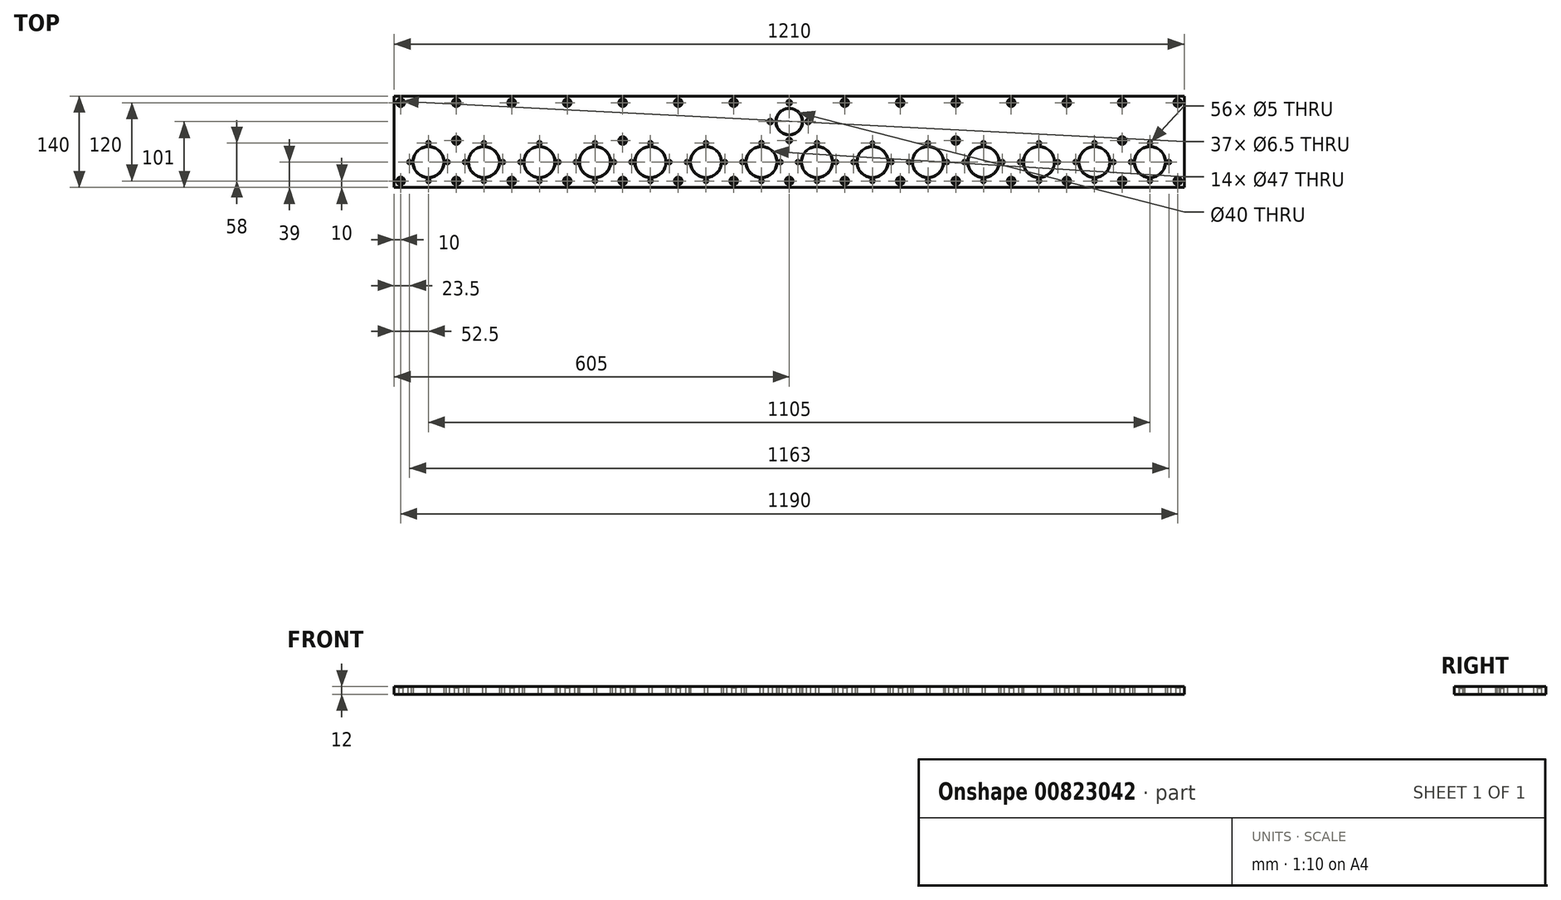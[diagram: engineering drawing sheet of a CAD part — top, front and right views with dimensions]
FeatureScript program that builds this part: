
annotation { "Feature Type Name" : "Feature", "Feature Type Description" : "" }
export const myFeature = defineFeature(function(context is Context, id is Id, definition is map)
    precondition{}
    {
        {
            var Q0;
            Q0=qCreatedBy(makeId("Top.planeOp"),FACE);
            var sketch = newSketch(context, id + "F0", { "sketchPlane" : qUnion([Q0])});
            skCircle(sketch, "E0", {"center": v(0, 0) * mm, "radius": 23.5 * mm, "construction": true});
            skLineSegment(sketch, "E1", {"start": v(0, 0) * mm, "end": v(1572.14, 0) * mm, "construction": true});
            skLineSegment(sketch, "E2", {"start": v(0, 0) * mm, "end": v(0, 543.6) * mm, "construction": true});
            skCircle(sketch, "E3", {"center": v(-42.5, -62) * mm, "radius": 23.5 * mm});
            skCircle(sketch, "E4", {"center": v(-42.5, -62) * mm, "radius": 37.5 * mm, "construction": true});
            skCircle(sketch, "E5", {"center": v(0, 0) * mm, "radius": 37.5 * mm, "construction": true});
            skCircle(sketch, "E6", {"center": v(-42.5, -62) * mm, "radius": 29 * mm, "construction": true});
            skCircle(sketch, "E7", {"center": v(0, 0) * mm, "radius": 29 * mm, "construction": true});
            skLineSegment(sketch, "E8", {"start": v(-42.5, -62) * mm, "end": v(-42.5, -24.5) * mm, "construction": true});
            skCircle(sketch, "E9", {"center": v(0, 29) * mm, "radius": 2.5 * mm, "construction": true});
            skCircle(sketch, "E10", {"center": v(-42.5, -33) * mm, "radius": 2.5 * mm});
            skCircle(sketch, "E11.1.0", {"center": v(-29, 0) * mm, "radius": 2.5 * mm, "construction": true});
            skCircle(sketch, "E11.2.0", {"center": v(0, -29) * mm, "radius": 2.5 * mm, "construction": true});
            skCircle(sketch, "E11.3.0", {"center": v(29, 0) * mm, "radius": 2.5 * mm, "construction": true});
            skLineSegment(sketch, "E12", {"start": v(-42.5, -62) * mm, "end": v(-80, -62) * mm, "construction": true});
            skLineSegment(sketch, "E13", {"start": v(-42.5, -62) * mm, "end": v(-42.5, -99.5) * mm, "construction": true});
            skLineSegment(sketch, "E14", {"start": v(-42.5, -62) * mm, "end": v(-5, -62) * mm, "construction": true});
            skCircle(sketch, "E15", {"center": v(-13.5, -62) * mm, "radius": 2.5 * mm});
            skCircle(sketch, "E16", {"center": v(-42.5, -91) * mm, "radius": 2.5 * mm});
            skCircle(sketch, "E17", {"center": v(-71.5, -62) * mm, "radius": 2.5 * mm});
            skCircle(sketch, "E18.MirrorC", {"center": v(42.5, -91) * mm, "radius": 2.5 * mm});
            skCircle(sketch, "E19.MirrorC", {"center": v(71.5, -62) * mm, "radius": 2.5 * mm});
            skCircle(sketch, "E20.MirrorC", {"center": v(42.5, -33) * mm, "radius": 2.5 * mm});
            skCircle(sketch, "E21.MirrorC", {"center": v(13.5, -62) * mm, "radius": 2.5 * mm});
            skCircle(sketch, "E22.MirrorC", {"center": v(42.5, -62) * mm, "radius": 23.5 * mm});
            skPoint(sketch, "E23.1.0.0", {"position": v(-85, 0) * mm});
            skCircle(sketch, "E23.1.0.1", {"center": v(-85, 0) * mm, "radius": 23.5 * mm, "construction": true});
            skCircle(sketch, "E23.1.0.2", {"center": v(-127.5, -62) * mm, "radius": 23.5 * mm});
            skCircle(sketch, "E23.1.0.3", {"center": v(-98.5, -62) * mm, "radius": 2.5 * mm});
            skCircle(sketch, "E23.1.0.4", {"center": v(-156.5, -62) * mm, "radius": 2.5 * mm});
            skCircle(sketch, "E23.1.0.5", {"center": v(-127.5, -91) * mm, "radius": 2.5 * mm});
            skCircle(sketch, "E23.1.0.6", {"center": v(-56, 0) * mm, "radius": 2.5 * mm, "construction": true});
            skCircle(sketch, "E23.1.0.7", {"center": v(-85, 29) * mm, "radius": 2.5 * mm, "construction": true});
            skCircle(sketch, "E23.1.0.8", {"center": v(-85, -29) * mm, "radius": 2.5 * mm, "construction": true});
            skCircle(sketch, "E23.1.0.9", {"center": v(-127.5, -33) * mm, "radius": 2.5 * mm});
            skCircle(sketch, "E23.1.0.10", {"center": v(-114, 0) * mm, "radius": 2.5 * mm, "construction": true});
            skPoint(sketch, "E23.2.0.0", {"position": v(-170, 0) * mm});
            skCircle(sketch, "E23.2.0.1", {"center": v(-170, 0) * mm, "radius": 23.5 * mm, "construction": true});
            skCircle(sketch, "E23.2.0.2", {"center": v(-212.5, -62) * mm, "radius": 23.5 * mm});
            skCircle(sketch, "E23.2.0.3", {"center": v(-183.5, -62) * mm, "radius": 2.5 * mm});
            skCircle(sketch, "E23.2.0.4", {"center": v(-241.5, -62) * mm, "radius": 2.5 * mm});
            skCircle(sketch, "E23.2.0.5", {"center": v(-212.5, -91) * mm, "radius": 2.5 * mm});
            skCircle(sketch, "E23.2.0.6", {"center": v(-141, 0) * mm, "radius": 2.5 * mm, "construction": true});
            skCircle(sketch, "E23.2.0.7", {"center": v(-170, 29) * mm, "radius": 2.5 * mm, "construction": true});
            skCircle(sketch, "E23.2.0.8", {"center": v(-170, -29) * mm, "radius": 2.5 * mm, "construction": true});
            skCircle(sketch, "E23.2.0.9", {"center": v(-212.5, -33) * mm, "radius": 2.5 * mm});
            skCircle(sketch, "E23.2.0.10", {"center": v(-199, 0) * mm, "radius": 2.5 * mm, "construction": true});
            skPoint(sketch, "E23.3.0.0", {"position": v(-255, 0) * mm});
            skCircle(sketch, "E23.3.0.1", {"center": v(-255, 0) * mm, "radius": 23.5 * mm, "construction": true});
            skCircle(sketch, "E23.3.0.2", {"center": v(-297.5, -62) * mm, "radius": 23.5 * mm});
            skCircle(sketch, "E23.3.0.3", {"center": v(-268.5, -62) * mm, "radius": 2.5 * mm});
            skCircle(sketch, "E23.3.0.4", {"center": v(-326.5, -62) * mm, "radius": 2.5 * mm});
            skCircle(sketch, "E23.3.0.5", {"center": v(-297.5, -91) * mm, "radius": 2.5 * mm});
            skCircle(sketch, "E23.3.0.6", {"center": v(-226, 0) * mm, "radius": 2.5 * mm, "construction": true});
            skCircle(sketch, "E23.3.0.7", {"center": v(-255, 29) * mm, "radius": 2.5 * mm, "construction": true});
            skCircle(sketch, "E23.3.0.8", {"center": v(-255, -29) * mm, "radius": 2.5 * mm, "construction": true});
            skCircle(sketch, "E23.3.0.9", {"center": v(-297.5, -33) * mm, "radius": 2.5 * mm});
            skCircle(sketch, "E23.3.0.10", {"center": v(-284, 0) * mm, "radius": 2.5 * mm, "construction": true});
            skPoint(sketch, "E23.4.0.0", {"position": v(-340, 0) * mm});
            skCircle(sketch, "E23.4.0.1", {"center": v(-340, 0) * mm, "radius": 23.5 * mm, "construction": true});
            skCircle(sketch, "E23.4.0.2", {"center": v(-382.5, -62) * mm, "radius": 23.5 * mm});
            skCircle(sketch, "E23.4.0.3", {"center": v(-353.5, -62) * mm, "radius": 2.5 * mm});
            skCircle(sketch, "E23.4.0.4", {"center": v(-411.5, -62) * mm, "radius": 2.5 * mm});
            skCircle(sketch, "E23.4.0.5", {"center": v(-382.5, -91) * mm, "radius": 2.5 * mm});
            skCircle(sketch, "E23.4.0.6", {"center": v(-311, 0) * mm, "radius": 2.5 * mm, "construction": true});
            skCircle(sketch, "E23.4.0.7", {"center": v(-340, 29) * mm, "radius": 2.5 * mm, "construction": true});
            skCircle(sketch, "E23.4.0.8", {"center": v(-340, -29) * mm, "radius": 2.5 * mm, "construction": true});
            skCircle(sketch, "E23.4.0.9", {"center": v(-382.5, -33) * mm, "radius": 2.5 * mm});
            skCircle(sketch, "E23.4.0.10", {"center": v(-369, 0) * mm, "radius": 2.5 * mm, "construction": true});
            skPoint(sketch, "E23.5.0.0", {"position": v(-425, 0) * mm});
            skCircle(sketch, "E23.5.0.1", {"center": v(-425, 0) * mm, "radius": 23.5 * mm, "construction": true});
            skCircle(sketch, "E23.5.0.2", {"center": v(-467.5, -62) * mm, "radius": 23.5 * mm});
            skCircle(sketch, "E23.5.0.3", {"center": v(-438.5, -62) * mm, "radius": 2.5 * mm});
            skCircle(sketch, "E23.5.0.4", {"center": v(-496.5, -62) * mm, "radius": 2.5 * mm});
            skCircle(sketch, "E23.5.0.5", {"center": v(-467.5, -91) * mm, "radius": 2.5 * mm});
            skCircle(sketch, "E23.5.0.6", {"center": v(-396, 0) * mm, "radius": 2.5 * mm, "construction": true});
            skCircle(sketch, "E23.5.0.7", {"center": v(-425, 29) * mm, "radius": 2.5 * mm, "construction": true});
            skCircle(sketch, "E23.5.0.8", {"center": v(-425, -29) * mm, "radius": 2.5 * mm, "construction": true});
            skCircle(sketch, "E23.5.0.9", {"center": v(-467.5, -33) * mm, "radius": 2.5 * mm});
            skCircle(sketch, "E23.5.0.10", {"center": v(-454, 0) * mm, "radius": 2.5 * mm, "construction": true});
            skPoint(sketch, "E23.6.0.0", {"position": v(-510, 0) * mm});
            skCircle(sketch, "E23.6.0.1", {"center": v(-510, 0) * mm, "radius": 23.5 * mm, "construction": true});
            skCircle(sketch, "E23.6.0.2", {"center": v(-552.5, -62) * mm, "radius": 23.5 * mm});
            skCircle(sketch, "E23.6.0.3", {"center": v(-523.5, -62) * mm, "radius": 2.5 * mm});
            skCircle(sketch, "E23.6.0.4", {"center": v(-581.5, -62) * mm, "radius": 2.5 * mm});
            skCircle(sketch, "E23.6.0.5", {"center": v(-552.5, -91) * mm, "radius": 2.5 * mm});
            skCircle(sketch, "E23.6.0.6", {"center": v(-481, 0) * mm, "radius": 2.5 * mm, "construction": true});
            skCircle(sketch, "E23.6.0.7", {"center": v(-510, 29) * mm, "radius": 2.5 * mm, "construction": true});
            skCircle(sketch, "E23.6.0.8", {"center": v(-510, -29) * mm, "radius": 2.5 * mm, "construction": true});
            skCircle(sketch, "E23.6.0.9", {"center": v(-552.5, -33) * mm, "radius": 2.5 * mm});
            skCircle(sketch, "E23.6.0.10", {"center": v(-539, 0) * mm, "radius": 2.5 * mm, "construction": true});
            skLineSegment(sketch, "E23.direction1", {"start": v(-42.5, -91) * mm, "end": v(-127.5, -91) * mm, "construction": true});
            skCircle(sketch, "E24.1.0.0", {"center": v(85, 0) * mm, "radius": 23.5 * mm, "construction": true});
            skCircle(sketch, "E24.1.0.1", {"center": v(85, -29) * mm, "radius": 2.5 * mm, "construction": true});
            skCircle(sketch, "E24.1.0.2", {"center": v(56, 0) * mm, "radius": 2.5 * mm, "construction": true});
            skCircle(sketch, "E24.1.0.3", {"center": v(85, 29) * mm, "radius": 2.5 * mm, "construction": true});
            skCircle(sketch, "E24.1.0.4", {"center": v(114, 0) * mm, "radius": 2.5 * mm, "construction": true});
            skCircle(sketch, "E24.1.0.5", {"center": v(127.5, -33) * mm, "radius": 2.5 * mm});
            skCircle(sketch, "E24.1.0.6", {"center": v(98.5, -62) * mm, "radius": 2.5 * mm});
            skCircle(sketch, "E24.1.0.7", {"center": v(127.5, -62) * mm, "radius": 23.5 * mm});
            skCircle(sketch, "E24.1.0.8", {"center": v(156.5, -62) * mm, "radius": 2.5 * mm});
            skCircle(sketch, "E24.1.0.9", {"center": v(127.5, -91) * mm, "radius": 2.5 * mm});
            skCircle(sketch, "E24.2.0.0", {"center": v(170, 0) * mm, "radius": 23.5 * mm, "construction": true});
            skCircle(sketch, "E24.2.0.1", {"center": v(170, -29) * mm, "radius": 2.5 * mm, "construction": true});
            skCircle(sketch, "E24.2.0.2", {"center": v(141, 0) * mm, "radius": 2.5 * mm, "construction": true});
            skCircle(sketch, "E24.2.0.3", {"center": v(170, 29) * mm, "radius": 2.5 * mm, "construction": true});
            skCircle(sketch, "E24.2.0.4", {"center": v(199, 0) * mm, "radius": 2.5 * mm, "construction": true});
            skCircle(sketch, "E24.2.0.5", {"center": v(212.5, -33) * mm, "radius": 2.5 * mm});
            skCircle(sketch, "E24.2.0.6", {"center": v(183.5, -62) * mm, "radius": 2.5 * mm});
            skCircle(sketch, "E24.2.0.7", {"center": v(212.5, -62) * mm, "radius": 23.5 * mm});
            skCircle(sketch, "E24.2.0.8", {"center": v(241.5, -62) * mm, "radius": 2.5 * mm});
            skCircle(sketch, "E24.2.0.9", {"center": v(212.5, -91) * mm, "radius": 2.5 * mm});
            skCircle(sketch, "E24.3.0.0", {"center": v(255, 0) * mm, "radius": 23.5 * mm, "construction": true});
            skCircle(sketch, "E24.3.0.1", {"center": v(255, -29) * mm, "radius": 2.5 * mm, "construction": true});
            skCircle(sketch, "E24.3.0.2", {"center": v(226, 0) * mm, "radius": 2.5 * mm, "construction": true});
            skCircle(sketch, "E24.3.0.3", {"center": v(255, 29) * mm, "radius": 2.5 * mm, "construction": true});
            skCircle(sketch, "E24.3.0.4", {"center": v(284, 0) * mm, "radius": 2.5 * mm, "construction": true});
            skCircle(sketch, "E24.3.0.5", {"center": v(297.5, -33) * mm, "radius": 2.5 * mm});
            skCircle(sketch, "E24.3.0.6", {"center": v(268.5, -62) * mm, "radius": 2.5 * mm});
            skCircle(sketch, "E24.3.0.7", {"center": v(297.5, -62) * mm, "radius": 23.5 * mm});
            skCircle(sketch, "E24.3.0.8", {"center": v(326.5, -62) * mm, "radius": 2.5 * mm});
            skCircle(sketch, "E24.3.0.9", {"center": v(297.5, -91) * mm, "radius": 2.5 * mm});
            skCircle(sketch, "E24.4.0.0", {"center": v(340, 0) * mm, "radius": 23.5 * mm, "construction": true});
            skCircle(sketch, "E24.4.0.1", {"center": v(340, -29) * mm, "radius": 2.5 * mm, "construction": true});
            skCircle(sketch, "E24.4.0.2", {"center": v(311, 0) * mm, "radius": 2.5 * mm, "construction": true});
            skCircle(sketch, "E24.4.0.3", {"center": v(340, 29) * mm, "radius": 2.5 * mm, "construction": true});
            skCircle(sketch, "E24.4.0.4", {"center": v(369, 0) * mm, "radius": 2.5 * mm, "construction": true});
            skCircle(sketch, "E24.4.0.5", {"center": v(382.5, -33) * mm, "radius": 2.5 * mm});
            skCircle(sketch, "E24.4.0.6", {"center": v(353.5, -62) * mm, "radius": 2.5 * mm});
            skCircle(sketch, "E24.4.0.7", {"center": v(382.5, -62) * mm, "radius": 23.5 * mm});
            skCircle(sketch, "E24.4.0.8", {"center": v(411.5, -62) * mm, "radius": 2.5 * mm});
            skCircle(sketch, "E24.4.0.9", {"center": v(382.5, -91) * mm, "radius": 2.5 * mm});
            skCircle(sketch, "E24.5.0.0", {"center": v(425, 0) * mm, "radius": 23.5 * mm, "construction": true});
            skCircle(sketch, "E24.5.0.1", {"center": v(425, -29) * mm, "radius": 2.5 * mm, "construction": true});
            skCircle(sketch, "E24.5.0.2", {"center": v(396, 0) * mm, "radius": 2.5 * mm, "construction": true});
            skCircle(sketch, "E24.5.0.3", {"center": v(425, 29) * mm, "radius": 2.5 * mm, "construction": true});
            skCircle(sketch, "E24.5.0.4", {"center": v(454, 0) * mm, "radius": 2.5 * mm, "construction": true});
            skCircle(sketch, "E24.5.0.5", {"center": v(467.5, -33) * mm, "radius": 2.5 * mm});
            skCircle(sketch, "E24.5.0.6", {"center": v(438.5, -62) * mm, "radius": 2.5 * mm});
            skCircle(sketch, "E24.5.0.7", {"center": v(467.5, -62) * mm, "radius": 23.5 * mm});
            skCircle(sketch, "E24.5.0.8", {"center": v(496.5, -62) * mm, "radius": 2.5 * mm});
            skCircle(sketch, "E24.5.0.9", {"center": v(467.5, -91) * mm, "radius": 2.5 * mm});
            skCircle(sketch, "E24.6.0.0", {"center": v(510, 0) * mm, "radius": 23.5 * mm, "construction": true});
            skCircle(sketch, "E24.6.0.1", {"center": v(510, -29) * mm, "radius": 2.5 * mm, "construction": true});
            skCircle(sketch, "E24.6.0.2", {"center": v(481, 0) * mm, "radius": 2.5 * mm, "construction": true});
            skCircle(sketch, "E24.6.0.3", {"center": v(510, 29) * mm, "radius": 2.5 * mm, "construction": true});
            skCircle(sketch, "E24.6.0.4", {"center": v(539, 0) * mm, "radius": 2.5 * mm, "construction": true});
            skCircle(sketch, "E24.6.0.5", {"center": v(552.5, -33) * mm, "radius": 2.5 * mm});
            skCircle(sketch, "E24.6.0.6", {"center": v(523.5, -62) * mm, "radius": 2.5 * mm});
            skCircle(sketch, "E24.6.0.7", {"center": v(552.5, -62) * mm, "radius": 23.5 * mm});
            skCircle(sketch, "E24.6.0.8", {"center": v(581.5, -62) * mm, "radius": 2.5 * mm});
            skCircle(sketch, "E24.6.0.9", {"center": v(552.5, -91) * mm, "radius": 2.5 * mm});
            skLineSegment(sketch, "E24.direction1", {"start": v(42.5, -91) * mm, "end": v(127.5, -91) * mm, "construction": true});
            skLineSegment(sketch, "E25.bottom", {"start": v(605, -101) * mm, "end": v(-605, -101) * mm});
            skLineSegment(sketch, "E25.top", {"start": v(605, 39) * mm, "end": v(-605, 39) * mm});
            skLineSegment(sketch, "E25.left", {"start": v(605, -101) * mm, "end": v(605, 39) * mm});
            skLineSegment(sketch, "E25.right", {"start": v(-605, -101) * mm, "end": v(-605, 39) * mm});
            skPoint(sketch, "E25.middle", {"position": v(0, -31) * mm});
            skLineSegment(sketch, "E26", {"start": v(-552.5, -62) * mm, "end": v(-510, 0) * mm, "construction": true});
            skLineSegment(sketch, "E27", {"start": v(-467.5, -62) * mm, "end": v(-510, 0) * mm, "construction": true});
            skLineSegment(sketch, "E28", {"start": v(-531.25, -31) * mm, "end": v(605, -31) * mm, "construction": true});
            skPoint(sketch, "E29.orphan", {"position": v(-488.75, -31) * mm});
            skCircle(sketch, "E30.MirrorC", {"center": v(-510, -91) * mm, "radius": 2.5 * mm, "construction": true});
            skCircle(sketch, "E31.MirrorC", {"center": v(-425, -91) * mm, "radius": 2.5 * mm, "construction": true});
            skLineSegment(sketch, "E32", {"start": v(-552.5, -62) * mm, "end": v(-552.5, 29.1) * mm, "construction": true});
            skCircle(sketch, "E33.MirrorC", {"center": v(-595, 29) * mm, "radius": 2.5 * mm, "construction": true});
            skCircle(sketch, "E34.MirrorC", {"center": v(-595, -91) * mm, "radius": 2.5 * mm, "construction": true});
            skCircle(sketch, "E35", {"center": v(-595, 29) * mm, "radius": 6 * mm, "construction": true});
            skCircle(sketch, "E36", {"center": v(-552.5, -62) * mm, "radius": 37 * mm, "construction": true});
            skCircle(sketch, "E37.MirrorC", {"center": v(510, -91) * mm, "radius": 2.5 * mm, "construction": true});
            skCircle(sketch, "E38.MirrorC", {"center": v(425, -91) * mm, "radius": 2.5 * mm, "construction": true});
            skLineSegment(sketch, "E39", {"start": v(552.5, -62) * mm, "end": v(552.5, 52.17) * mm, "construction": true});
            skCircle(sketch, "E40.MirrorC", {"center": v(595, 29) * mm, "radius": 2.5 * mm, "construction": true});
            skCircle(sketch, "E41.MirrorC", {"center": v(595, -91) * mm, "radius": 2.5 * mm, "construction": true});
            skCircle(sketch, "E42.MirrorC", {"center": v(340, -91) * mm, "radius": 2.5 * mm, "construction": true});
            skCircle(sketch, "E43.MirrorC", {"center": v(255, -91) * mm, "radius": 2.5 * mm, "construction": true});
            skCircle(sketch, "E44.MirrorC", {"center": v(170, -91) * mm, "radius": 2.5 * mm, "construction": true});
            skCircle(sketch, "E45.MirrorC", {"center": v(85, -91) * mm, "radius": 2.5 * mm, "construction": true});
            skCircle(sketch, "E46.MirrorC", {"center": v(0, -91) * mm, "radius": 2.5 * mm, "construction": true});
            skCircle(sketch, "E47.MirrorC", {"center": v(-85, -91) * mm, "radius": 2.5 * mm, "construction": true});
            skCircle(sketch, "E48.MirrorC", {"center": v(-170, -91) * mm, "radius": 2.5 * mm, "construction": true});
            skCircle(sketch, "E49.MirrorC", {"center": v(-255, -91) * mm, "radius": 2.5 * mm, "construction": true});
            skCircle(sketch, "E50.MirrorC", {"center": v(-340, -91) * mm, "radius": 2.5 * mm, "construction": true});
            skCircle(sketch, "E51", {"center": v(-595, 29) * mm, "radius": 3.25 * mm});
            skCircle(sketch, "E52", {"center": v(-595, -91) * mm, "radius": 3.25 * mm});
            skCircle(sketch, "E53.1.0.0", {"center": v(-510, 29) * mm, "radius": 3.25 * mm});
            skCircle(sketch, "E53.1.0.1", {"center": v(-510, -91) * mm, "radius": 3.25 * mm});
            skCircle(sketch, "E53.2.0.0", {"center": v(-425, 29) * mm, "radius": 3.25 * mm});
            skCircle(sketch, "E53.2.0.1", {"center": v(-425, -91) * mm, "radius": 3.25 * mm});
            skCircle(sketch, "E53.3.0.0", {"center": v(-340, 29) * mm, "radius": 3.25 * mm});
            skCircle(sketch, "E53.3.0.1", {"center": v(-340, -91) * mm, "radius": 3.25 * mm});
            skCircle(sketch, "E53.4.0.0", {"center": v(-255, 29) * mm, "radius": 3.25 * mm});
            skCircle(sketch, "E53.4.0.1", {"center": v(-255, -91) * mm, "radius": 3.25 * mm});
            skCircle(sketch, "E53.5.0.0", {"center": v(-170, 29) * mm, "radius": 3.25 * mm});
            skCircle(sketch, "E53.5.0.1", {"center": v(-170, -91) * mm, "radius": 3.25 * mm});
            skCircle(sketch, "E53.6.0.0", {"center": v(-85, 29) * mm, "radius": 3.25 * mm});
            skCircle(sketch, "E53.6.0.1", {"center": v(-85, -91) * mm, "radius": 3.25 * mm});
            skCircle(sketch, "E53.7.0.0", {"center": v(0, 29) * mm, "radius": 3.25 * mm});
            skCircle(sketch, "E53.7.0.1", {"center": v(0, -91) * mm, "radius": 3.25 * mm});
            skCircle(sketch, "E53.8.0.0", {"center": v(85, 29) * mm, "radius": 3.25 * mm});
            skCircle(sketch, "E53.8.0.1", {"center": v(85, -91) * mm, "radius": 3.25 * mm});
            skCircle(sketch, "E53.9.0.0", {"center": v(170, 29) * mm, "radius": 3.25 * mm});
            skCircle(sketch, "E53.9.0.1", {"center": v(170, -91) * mm, "radius": 3.25 * mm});
            skCircle(sketch, "E53.10.0.0", {"center": v(255, 29) * mm, "radius": 3.25 * mm});
            skCircle(sketch, "E53.10.0.1", {"center": v(255, -91) * mm, "radius": 3.25 * mm});
            skCircle(sketch, "E53.11.0.0", {"center": v(340, 29) * mm, "radius": 3.25 * mm});
            skCircle(sketch, "E53.11.0.1", {"center": v(340, -91) * mm, "radius": 3.25 * mm});
            skCircle(sketch, "E53.12.0.0", {"center": v(425, 29) * mm, "radius": 3.25 * mm});
            skCircle(sketch, "E53.12.0.1", {"center": v(425, -91) * mm, "radius": 3.25 * mm});
            skCircle(sketch, "E53.13.0.0", {"center": v(510, 29) * mm, "radius": 3.25 * mm});
            skCircle(sketch, "E53.13.0.1", {"center": v(510, -91) * mm, "radius": 3.25 * mm});
            skCircle(sketch, "E53.14.0.0", {"center": v(595, 29) * mm, "radius": 3.25 * mm});
            skCircle(sketch, "E53.14.0.1", {"center": v(595, -91) * mm, "radius": 3.25 * mm});
            skLineSegment(sketch, "E53.direction1", {"start": v(-595, -91) * mm, "end": v(-510, -91) * mm, "construction": true});
            skCircle(sketch, "E54", {"center": v(-510, -29) * mm, "radius": 3.25 * mm});
            skCircle(sketch, "E55", {"center": v(0, -29) * mm, "radius": 3.25 * mm});
            skCircle(sketch, "E56", {"center": v(510, -29) * mm, "radius": 3.25 * mm});
            skCircle(sketch, "E57", {"center": v(255, -29) * mm, "radius": 3.25 * mm});
            skCircle(sketch, "E58", {"center": v(-255, -29) * mm, "radius": 3.25 * mm});
            skCircle(sketch, "E59", {"center": v(-29, 0) * mm, "radius": 3.25 * mm});
            skCircle(sketch, "E60", {"center": v(29, 0) * mm, "radius": 3.25 * mm});
            skCircle(sketch, "E61", {"center": v(0, 0) * mm, "radius": 20 * mm});
            skSolve(sketch);
        }
        {
            var Q0;
            Q0=qSketchRegion(id+"F0",true);
            extrude(context, id + "F1", {"entities" : qUnion([Q0]), "depth" : 12 * mm, "offsetDistance" : 25 * mm});
        }
        {
            var Q0;
            Q0=makeQuery(id+"F1.opExtrude","SWEPT_FACE",FACE,{"disambiguationData":[OSD([sQuery(id+"F0.wireOp",EDGE,"E24.6.0.7")])]});
            var Q1;
            Q1=makeQuery(id+"F1.opExtrude","SWEPT_FACE",FACE,{"disambiguationData":[OSD([sQuery(id+"F0.wireOp",EDGE,"E24.6.0.6")])]});
            var Q2;
            Q2=makeQuery(id+"F1.opExtrude","SWEPT_FACE",FACE,{"disambiguationData":[OSD([sQuery(id+"F0.wireOp",EDGE,"E24.6.0.9")])]});
            var Q3;
            Q3=makeQuery(id+"F1.opExtrude","SWEPT_FACE",FACE,{"disambiguationData":[OSD([sQuery(id+"F0.wireOp",EDGE,"E24.6.0.5")])]});
            var Q4;
            Q4=makeQuery(id+"F1.opExtrude","SWEPT_FACE",FACE,{"disambiguationData":[OSD([sQuery(id+"F0.wireOp",EDGE,"E24.6.0.8")])]});
            var Q5;
            Q5=makeQuery(id+"F1.opExtrude","SWEPT_FACE",FACE,{"disambiguationData":[OSD([sQuery(id+"F0.wireOp",EDGE,"E24.5.0.7")])]});
            var Q6;
            Q6=makeQuery(id+"F1.opExtrude","SWEPT_FACE",FACE,{"disambiguationData":[OSD([sQuery(id+"F0.wireOp",EDGE,"E24.6.0.0")])]});
            var Q7;
            Q7=makeQuery(id+"F1.opExtrude","SWEPT_FACE",FACE,{"disambiguationData":[OSD([sQuery(id+"F0.wireOp",EDGE,"E24.5.0.0")])]});
            var Q8;
            Q8=makeQuery(id+"F1.opExtrude","SWEPT_FACE",FACE,{"disambiguationData":[OSD([sQuery(id+"F0.wireOp",EDGE,"E24.4.0.7")])]});
            var Q9;
            Q9=makeQuery(id+"F1.opExtrude","SWEPT_FACE",FACE,{"disambiguationData":[OSD([sQuery(id+"F0.wireOp",EDGE,"E24.3.0.7")])]});
            var Q10;
            Q10=makeQuery(id+"F1.opExtrude","SWEPT_FACE",FACE,{"disambiguationData":[OSD([sQuery(id+"F0.wireOp",EDGE,"E24.4.0.0")])]});
            var Q11;
            Q11=makeQuery(id+"F1.opExtrude","SWEPT_FACE",FACE,{"disambiguationData":[OSD([sQuery(id+"F0.wireOp",EDGE,"E24.3.0.0")])]});
            var Q12;
            Q12=makeQuery(id+"F1.opExtrude","SWEPT_FACE",FACE,{"disambiguationData":[OSD([sQuery(id+"F0.wireOp",EDGE,"E24.2.0.7")])]});
            var Q13;
            Q13=makeQuery(id+"F1.opExtrude","SWEPT_FACE",FACE,{"disambiguationData":[OSD([sQuery(id+"F0.wireOp",EDGE,"E24.2.0.0")])]});
            var Q14;
            Q14=makeQuery(id+"F1.opExtrude","SWEPT_FACE",FACE,{"disambiguationData":[OSD([sQuery(id+"F0.wireOp",EDGE,"E24.1.0.7")])]});
            var Q15;
            Q15=makeQuery(id+"F1.opExtrude","SWEPT_FACE",FACE,{"disambiguationData":[OSD([sQuery(id+"F0.wireOp",EDGE,"E24.1.0.0")])]});
            var Q16;
            Q16=makeQuery(id+"F1.opExtrude","SWEPT_FACE",FACE,{"disambiguationData":[OSD([sQuery(id+"F0.wireOp",EDGE,"E22.MirrorC")])]});
            var Q17;
            Q17=makeQuery(id+"F1.opExtrude","SWEPT_FACE",FACE,{"disambiguationData":[OSD([sQuery(id+"F0.wireOp",EDGE,"E0")])]});
            var Q18;
            Q18=makeQuery(id+"F1.opExtrude","SWEPT_FACE",FACE,{"disambiguationData":[OSD([sQuery(id+"F0.wireOp",EDGE,"E3")])]});
            var Q19;
            Q19=makeQuery(id+"F1.opExtrude","SWEPT_FACE",FACE,{"disambiguationData":[OSD([sQuery(id+"F0.wireOp",EDGE,"E23.1.0.1")])]});
            var Q20;
            Q20=makeQuery(id+"F1.opExtrude","SWEPT_FACE",FACE,{"disambiguationData":[OSD([sQuery(id+"F0.wireOp",EDGE,"E23.1.0.2")])]});
            var Q21;
            Q21=makeQuery(id+"F1.opExtrude","SWEPT_FACE",FACE,{"disambiguationData":[OSD([sQuery(id+"F0.wireOp",EDGE,"E23.2.0.1")])]});
            var Q22;
            Q22=makeQuery(id+"F1.opExtrude","SWEPT_FACE",FACE,{"disambiguationData":[OSD([sQuery(id+"F0.wireOp",EDGE,"E23.2.0.2")])]});
            var Q23;
            Q23=makeQuery(id+"F1.opExtrude","SWEPT_FACE",FACE,{"disambiguationData":[OSD([sQuery(id+"F0.wireOp",EDGE,"E23.3.0.1")])]});
            var Q24;
            Q24=makeQuery(id+"F1.opExtrude","SWEPT_FACE",FACE,{"disambiguationData":[OSD([sQuery(id+"F0.wireOp",EDGE,"E23.3.0.2")])]});
            var Q25;
            Q25=makeQuery(id+"F1.opExtrude","SWEPT_FACE",FACE,{"disambiguationData":[OSD([sQuery(id+"F0.wireOp",EDGE,"E23.4.0.1")])]});
            var Q26;
            Q26=makeQuery(id+"F1.opExtrude","SWEPT_FACE",FACE,{"disambiguationData":[OSD([sQuery(id+"F0.wireOp",EDGE,"E23.4.0.2")])]});
            var Q27;
            Q27=makeQuery(id+"F1.opExtrude","SWEPT_FACE",FACE,{"disambiguationData":[OSD([sQuery(id+"F0.wireOp",EDGE,"E23.5.0.1")])]});
            var Q28;
            Q28=makeQuery(id+"F1.opExtrude","SWEPT_FACE",FACE,{"disambiguationData":[OSD([sQuery(id+"F0.wireOp",EDGE,"E23.5.0.2")])]});
            var Q29;
            Q29=makeQuery(id+"F1.opExtrude","SWEPT_FACE",FACE,{"disambiguationData":[OSD([sQuery(id+"F0.wireOp",EDGE,"E23.6.0.1")])]});
            var Q30;
            Q30=makeQuery(id+"F1.opExtrude","SWEPT_FACE",FACE,{"disambiguationData":[OSD([sQuery(id+"F0.wireOp",EDGE,"E23.6.0.2")])]});
            var Q31;
            Q31=makeQuery(id+"F1.opExtrude","SWEPT_FACE",FACE,{"disambiguationData":[OSD([sQuery(id+"F0.wireOp",EDGE,"E23.6.0.4")])]});
            var Q32;
            Q32=makeQuery(id+"F1.opExtrude","SWEPT_FACE",FACE,{"disambiguationData":[OSD([sQuery(id+"F0.wireOp",EDGE,"E23.6.0.5")])]});
            var Q33;
            Q33=makeQuery(id+"F1.opExtrude","SWEPT_FACE",FACE,{"disambiguationData":[OSD([sQuery(id+"F0.wireOp",EDGE,"E23.6.0.3")])]});
            var Q34;
            Q34=makeQuery(id+"F1.opExtrude","SWEPT_FACE",FACE,{"disambiguationData":[OSD([sQuery(id+"F0.wireOp",EDGE,"E23.6.0.9")])]});
            var Q35;
            Q35=makeQuery(id+"F1.opExtrude","SWEPT_FACE",FACE,{"disambiguationData":[OSD([sQuery(id+"F0.wireOp",EDGE,"E23.6.0.8")])]});
            var Q36;
            Q36=makeQuery(id+"F1.opExtrude","SWEPT_FACE",FACE,{"disambiguationData":[OSD([sQuery(id+"F0.wireOp",EDGE,"E23.6.0.10")])]});
            var Q37;
            Q37=makeQuery(id+"F1.opExtrude","SWEPT_FACE",FACE,{"disambiguationData":[OSD([sQuery(id+"F0.wireOp",EDGE,"E23.6.0.7")])]});
            var Q38;
            Q38=makeQuery(id+"F1.opExtrude","SWEPT_FACE",FACE,{"disambiguationData":[OSD([sQuery(id+"F0.wireOp",EDGE,"E23.6.0.6")])]});
            var Q39;
            Q39=makeQuery(id+"F1.opExtrude","SWEPT_FACE",FACE,{"disambiguationData":[OSD([sQuery(id+"F0.wireOp",EDGE,"E24.6.0.4")])]});
            var Q40;
            Q40=makeQuery(id+"F1.opExtrude","SWEPT_FACE",FACE,{"disambiguationData":[OSD([sQuery(id+"F0.wireOp",EDGE,"E24.6.0.1")])]});
            var Q41;
            Q41=makeQuery(id+"F1.opExtrude","SWEPT_FACE",FACE,{"disambiguationData":[OSD([sQuery(id+"F0.wireOp",EDGE,"E24.6.0.2")])]});
            var Q42;
            Q42=makeQuery(id+"F1.opExtrude","SWEPT_FACE",FACE,{"disambiguationData":[OSD([sQuery(id+"F0.wireOp",EDGE,"E24.6.0.3")])]});
            var Q43;
            Q43=makeQuery(id+"F1.opExtrude","SWEPT_FACE",FACE,{"disambiguationData":[OSD([sQuery(id+"F0.wireOp",EDGE,"E61")])]});
            chamfer(context, id + "F2", {"entities" : qUnion([Q0, Q1, Q2, Q3, Q4, Q5, Q6, Q7, Q8, Q9, Q10, Q11, Q12, Q13, Q14, Q15, Q16, Q17, Q18, Q19, Q20, Q21, Q22, Q23, Q24, Q25, Q26, Q27, Q28, Q29, Q30, Q31, Q32, Q33, Q34, Q35, Q36, Q37, Q38, Q39, Q40, Q41, Q42, Q43]), "width" : 0.5 * mm, "tangentPropagation" : true});
        }
        {
            var Q0;
            Q0=makeQuery(id+"F1.opExtrude","SWEPT_FACE",FACE,{"disambiguationData":[OSD([sQuery(id+"F0.wireOp",EDGE,"E24.5.0.9")])]});
            var Q1;
            Q1=makeQuery(id+"F1.opExtrude","SWEPT_FACE",FACE,{"disambiguationData":[OSD([sQuery(id+"F0.wireOp",EDGE,"E24.5.0.6")])]});
            var Q2;
            Q2=makeQuery(id+"F1.opExtrude","SWEPT_FACE",FACE,{"disambiguationData":[OSD([sQuery(id+"F0.wireOp",EDGE,"E24.5.0.5")])]});
            var Q3;
            Q3=makeQuery(id+"F1.opExtrude","SWEPT_FACE",FACE,{"disambiguationData":[OSD([sQuery(id+"F0.wireOp",EDGE,"E24.5.0.8")])]});
            var Q4;
            Q4=makeQuery(id+"F1.opExtrude","SWEPT_FACE",FACE,{"disambiguationData":[OSD([sQuery(id+"F0.wireOp",EDGE,"E24.5.0.1")])]});
            var Q5;
            Q5=makeQuery(id+"F1.opExtrude","SWEPT_FACE",FACE,{"disambiguationData":[OSD([sQuery(id+"F0.wireOp",EDGE,"E24.5.0.2")])]});
            var Q6;
            Q6=makeQuery(id+"F1.opExtrude","SWEPT_FACE",FACE,{"disambiguationData":[OSD([sQuery(id+"F0.wireOp",EDGE,"E24.5.0.3")])]});
            var Q7;
            Q7=makeQuery(id+"F1.opExtrude","SWEPT_FACE",FACE,{"disambiguationData":[OSD([sQuery(id+"F0.wireOp",EDGE,"E24.5.0.4")])]});
            var Q8;
            Q8=makeQuery(id+"F1.opExtrude","SWEPT_FACE",FACE,{"disambiguationData":[OSD([sQuery(id+"F0.wireOp",EDGE,"E24.4.0.6")])]});
            var Q9;
            Q9=makeQuery(id+"F1.opExtrude","SWEPT_FACE",FACE,{"disambiguationData":[OSD([sQuery(id+"F0.wireOp",EDGE,"E24.4.0.9")])]});
            var Q10;
            Q10=makeQuery(id+"F1.opExtrude","SWEPT_FACE",FACE,{"disambiguationData":[OSD([sQuery(id+"F0.wireOp",EDGE,"E24.4.0.5")])]});
            var Q11;
            Q11=makeQuery(id+"F1.opExtrude","SWEPT_FACE",FACE,{"disambiguationData":[OSD([sQuery(id+"F0.wireOp",EDGE,"E24.4.0.8")])]});
            var Q12;
            Q12=makeQuery(id+"F1.opExtrude","SWEPT_FACE",FACE,{"disambiguationData":[OSD([sQuery(id+"F0.wireOp",EDGE,"E24.4.0.1")])]});
            var Q13;
            Q13=makeQuery(id+"F1.opExtrude","SWEPT_FACE",FACE,{"disambiguationData":[OSD([sQuery(id+"F0.wireOp",EDGE,"E24.4.0.2")])]});
            var Q14;
            Q14=makeQuery(id+"F1.opExtrude","SWEPT_FACE",FACE,{"disambiguationData":[OSD([sQuery(id+"F0.wireOp",EDGE,"E24.4.0.3")])]});
            var Q15;
            Q15=makeQuery(id+"F1.opExtrude","SWEPT_FACE",FACE,{"disambiguationData":[OSD([sQuery(id+"F0.wireOp",EDGE,"E24.4.0.4")])]});
            var Q16;
            Q16=makeQuery(id+"F1.opExtrude","SWEPT_FACE",FACE,{"disambiguationData":[OSD([sQuery(id+"F0.wireOp",EDGE,"E24.3.0.9")])]});
            var Q17;
            Q17=makeQuery(id+"F1.opExtrude","SWEPT_FACE",FACE,{"disambiguationData":[OSD([sQuery(id+"F0.wireOp",EDGE,"E24.3.0.6")])]});
            var Q18;
            Q18=makeQuery(id+"F1.opExtrude","SWEPT_FACE",FACE,{"disambiguationData":[OSD([sQuery(id+"F0.wireOp",EDGE,"E24.3.0.5")])]});
            var Q19;
            Q19=makeQuery(id+"F1.opExtrude","SWEPT_FACE",FACE,{"disambiguationData":[OSD([sQuery(id+"F0.wireOp",EDGE,"E24.3.0.8")])]});
            var Q20;
            Q20=makeQuery(id+"F1.opExtrude","SWEPT_FACE",FACE,{"disambiguationData":[OSD([sQuery(id+"F0.wireOp",EDGE,"E24.3.0.1")])]});
            var Q21;
            Q21=makeQuery(id+"F1.opExtrude","SWEPT_FACE",FACE,{"disambiguationData":[OSD([sQuery(id+"F0.wireOp",EDGE,"E24.3.0.2")])]});
            var Q22;
            Q22=makeQuery(id+"F1.opExtrude","SWEPT_FACE",FACE,{"disambiguationData":[OSD([sQuery(id+"F0.wireOp",EDGE,"E24.3.0.4")])]});
            var Q23;
            Q23=makeQuery(id+"F1.opExtrude","SWEPT_FACE",FACE,{"disambiguationData":[OSD([sQuery(id+"F0.wireOp",EDGE,"E24.3.0.3")])]});
            var Q24;
            Q24=makeQuery(id+"F1.opExtrude","SWEPT_FACE",FACE,{"disambiguationData":[OSD([sQuery(id+"F0.wireOp",EDGE,"E24.2.0.6")])]});
            var Q25;
            Q25=makeQuery(id+"F1.opExtrude","SWEPT_FACE",FACE,{"disambiguationData":[OSD([sQuery(id+"F0.wireOp",EDGE,"E24.2.0.9")])]});
            var Q26;
            Q26=makeQuery(id+"F1.opExtrude","SWEPT_FACE",FACE,{"disambiguationData":[OSD([sQuery(id+"F0.wireOp",EDGE,"E24.2.0.8")])]});
            var Q27;
            Q27=makeQuery(id+"F1.opExtrude","SWEPT_FACE",FACE,{"disambiguationData":[OSD([sQuery(id+"F0.wireOp",EDGE,"E24.2.0.5")])]});
            var Q28;
            Q28=makeQuery(id+"F1.opExtrude","SWEPT_FACE",FACE,{"disambiguationData":[OSD([sQuery(id+"F0.wireOp",EDGE,"E24.2.0.1")])]});
            var Q29;
            Q29=makeQuery(id+"F1.opExtrude","SWEPT_FACE",FACE,{"disambiguationData":[OSD([sQuery(id+"F0.wireOp",EDGE,"E24.2.0.2")])]});
            var Q30;
            Q30=makeQuery(id+"F1.opExtrude","SWEPT_FACE",FACE,{"disambiguationData":[OSD([sQuery(id+"F0.wireOp",EDGE,"E24.2.0.3")])]});
            var Q31;
            Q31=makeQuery(id+"F1.opExtrude","SWEPT_FACE",FACE,{"disambiguationData":[OSD([sQuery(id+"F0.wireOp",EDGE,"E24.2.0.4")])]});
            var Q32;
            Q32=makeQuery(id+"F1.opExtrude","SWEPT_FACE",FACE,{"disambiguationData":[OSD([sQuery(id+"F0.wireOp",EDGE,"E24.1.0.6")])]});
            var Q33;
            Q33=makeQuery(id+"F1.opExtrude","SWEPT_FACE",FACE,{"disambiguationData":[OSD([sQuery(id+"F0.wireOp",EDGE,"E24.1.0.9")])]});
            var Q34;
            Q34=makeQuery(id+"F1.opExtrude","CAP_EDGE",EDGE,{"disambiguationData":[OSD([sQuery(id+"F0.wireOp",EDGE,"E24.1.0.5")])],"isStart":true});
            var Q35;
            Q35=makeQuery(id+"F1.opExtrude","SWEPT_FACE",FACE,{"disambiguationData":[OSD([sQuery(id+"F0.wireOp",EDGE,"E24.1.0.8")])]});
            var Q36;
            Q36=makeQuery(id+"F1.opExtrude","SWEPT_FACE",FACE,{"disambiguationData":[OSD([sQuery(id+"F0.wireOp",EDGE,"E24.1.0.1")])]});
            var Q37;
            Q37=makeQuery(id+"F1.opExtrude","SWEPT_FACE",FACE,{"disambiguationData":[OSD([sQuery(id+"F0.wireOp",EDGE,"E24.1.0.2")])]});
            var Q38;
            Q38=makeQuery(id+"F1.opExtrude","SWEPT_FACE",FACE,{"disambiguationData":[OSD([sQuery(id+"F0.wireOp",EDGE,"E24.1.0.3")])]});
            var Q39;
            Q39=makeQuery(id+"F1.opExtrude","SWEPT_FACE",FACE,{"disambiguationData":[OSD([sQuery(id+"F0.wireOp",EDGE,"E24.1.0.4")])]});
            var Q40;
            Q40=makeQuery(id+"F1.opExtrude","SWEPT_FACE",FACE,{"disambiguationData":[OSD([sQuery(id+"F0.wireOp",EDGE,"E21.MirrorC")])]});
            var Q41;
            Q41=makeQuery(id+"F1.opExtrude","SWEPT_FACE",FACE,{"disambiguationData":[OSD([sQuery(id+"F0.wireOp",EDGE,"E18.MirrorC")])]});
            var Q42;
            Q42=makeQuery(id+"F1.opExtrude","SWEPT_FACE",FACE,{"disambiguationData":[OSD([sQuery(id+"F0.wireOp",EDGE,"E20.MirrorC")])]});
            var Q43;
            Q43=makeQuery(id+"F1.opExtrude","SWEPT_FACE",FACE,{"disambiguationData":[OSD([sQuery(id+"F0.wireOp",EDGE,"E19.MirrorC")])]});
            var Q44;
            Q44=makeQuery(id+"F1.opExtrude","SWEPT_FACE",FACE,{"disambiguationData":[OSD([sQuery(id+"F0.wireOp",EDGE,"E11.2.0")])]});
            var Q45;
            Q45=makeQuery(id+"F1.opExtrude","SWEPT_FACE",FACE,{"disambiguationData":[OSD([sQuery(id+"F0.wireOp",EDGE,"E11.1.0")])]});
            var Q46;
            Q46=makeQuery(id+"F1.opExtrude","SWEPT_FACE",FACE,{"disambiguationData":[OSD([sQuery(id+"F0.wireOp",EDGE,"E9")])]});
            var Q47;
            Q47=makeQuery(id+"F1.opExtrude","SWEPT_FACE",FACE,{"disambiguationData":[OSD([sQuery(id+"F0.wireOp",EDGE,"E11.3.0")])]});
            var Q48;
            Q48=makeQuery(id+"F1.opExtrude","SWEPT_FACE",FACE,{"disambiguationData":[OSD([sQuery(id+"F0.wireOp",EDGE,"E17")])]});
            var Q49;
            Q49=makeQuery(id+"F1.opExtrude","SWEPT_FACE",FACE,{"disambiguationData":[OSD([sQuery(id+"F0.wireOp",EDGE,"E16")])]});
            var Q50;
            Q50=makeQuery(id+"F1.opExtrude","SWEPT_FACE",FACE,{"disambiguationData":[OSD([sQuery(id+"F0.wireOp",EDGE,"E15")])]});
            var Q51;
            Q51=makeQuery(id+"F1.opExtrude","SWEPT_FACE",FACE,{"disambiguationData":[OSD([sQuery(id+"F0.wireOp",EDGE,"E10")])]});
            var Q52;
            Q52=makeQuery(id+"F1.opExtrude","SWEPT_FACE",FACE,{"disambiguationData":[OSD([sQuery(id+"F0.wireOp",EDGE,"E23.1.0.8")])]});
            var Q53;
            Q53=makeQuery(id+"F1.opExtrude","SWEPT_FACE",FACE,{"disambiguationData":[OSD([sQuery(id+"F0.wireOp",EDGE,"E23.1.0.10")])]});
            var Q54;
            Q54=makeQuery(id+"F1.opExtrude","SWEPT_FACE",FACE,{"disambiguationData":[OSD([sQuery(id+"F0.wireOp",EDGE,"E23.1.0.7")])]});
            var Q55;
            Q55=makeQuery(id+"F1.opExtrude","SWEPT_FACE",FACE,{"disambiguationData":[OSD([sQuery(id+"F0.wireOp",EDGE,"E23.1.0.6")])]});
            var Q56;
            Q56=makeQuery(id+"F1.opExtrude","SWEPT_FACE",FACE,{"disambiguationData":[OSD([sQuery(id+"F0.wireOp",EDGE,"E23.1.0.9")])]});
            var Q57;
            Q57=makeQuery(id+"F1.opExtrude","SWEPT_FACE",FACE,{"disambiguationData":[OSD([sQuery(id+"F0.wireOp",EDGE,"E23.1.0.4")])]});
            var Q58;
            Q58=makeQuery(id+"F1.opExtrude","SWEPT_FACE",FACE,{"disambiguationData":[OSD([sQuery(id+"F0.wireOp",EDGE,"E23.1.0.5")])]});
            var Q59;
            Q59=makeQuery(id+"F1.opExtrude","SWEPT_FACE",FACE,{"disambiguationData":[OSD([sQuery(id+"F0.wireOp",EDGE,"E23.1.0.3")])]});
            var Q60;
            Q60=makeQuery(id+"F1.opExtrude","SWEPT_FACE",FACE,{"disambiguationData":[OSD([sQuery(id+"F0.wireOp",EDGE,"E23.2.0.9")])]});
            var Q61;
            Q61=makeQuery(id+"F1.opExtrude","SWEPT_FACE",FACE,{"disambiguationData":[OSD([sQuery(id+"F0.wireOp",EDGE,"E23.2.0.4")])]});
            var Q62;
            Q62=makeQuery(id+"F1.opExtrude","SWEPT_FACE",FACE,{"disambiguationData":[OSD([sQuery(id+"F0.wireOp",EDGE,"E23.2.0.5")])]});
            var Q63;
            Q63=makeQuery(id+"F1.opExtrude","SWEPT_FACE",FACE,{"disambiguationData":[OSD([sQuery(id+"F0.wireOp",EDGE,"E23.2.0.3")])]});
            var Q64;
            Q64=makeQuery(id+"F1.opExtrude","SWEPT_FACE",FACE,{"disambiguationData":[OSD([sQuery(id+"F0.wireOp",EDGE,"E23.2.0.8")])]});
            var Q65;
            Q65=makeQuery(id+"F1.opExtrude","SWEPT_FACE",FACE,{"disambiguationData":[OSD([sQuery(id+"F0.wireOp",EDGE,"E23.2.0.10")])]});
            var Q66;
            Q66=makeQuery(id+"F1.opExtrude","SWEPT_FACE",FACE,{"disambiguationData":[OSD([sQuery(id+"F0.wireOp",EDGE,"E23.2.0.7")])]});
            var Q67;
            Q67=makeQuery(id+"F1.opExtrude","SWEPT_FACE",FACE,{"disambiguationData":[OSD([sQuery(id+"F0.wireOp",EDGE,"E23.2.0.6")])]});
            var Q68;
            Q68=makeQuery(id+"F1.opExtrude","SWEPT_FACE",FACE,{"disambiguationData":[OSD([sQuery(id+"F0.wireOp",EDGE,"E23.3.0.10")])]});
            var Q69;
            Q69=makeQuery(id+"F1.opExtrude","SWEPT_FACE",FACE,{"disambiguationData":[OSD([sQuery(id+"F0.wireOp",EDGE,"E23.3.0.8")])]});
            var Q70;
            Q70=makeQuery(id+"F1.opExtrude","SWEPT_FACE",FACE,{"disambiguationData":[OSD([sQuery(id+"F0.wireOp",EDGE,"E23.3.0.7")])]});
            var Q71;
            Q71=makeQuery(id+"F1.opExtrude","SWEPT_FACE",FACE,{"disambiguationData":[OSD([sQuery(id+"F0.wireOp",EDGE,"E23.3.0.6")])]});
            var Q72;
            Q72=makeQuery(id+"F1.opExtrude","SWEPT_FACE",FACE,{"disambiguationData":[OSD([sQuery(id+"F0.wireOp",EDGE,"E23.4.0.7")])]});
            var Q73;
            Q73=makeQuery(id+"F1.opExtrude","SWEPT_FACE",FACE,{"disambiguationData":[OSD([sQuery(id+"F0.wireOp",EDGE,"E23.4.0.10")])]});
            var Q74;
            Q74=makeQuery(id+"F1.opExtrude","SWEPT_FACE",FACE,{"disambiguationData":[OSD([sQuery(id+"F0.wireOp",EDGE,"E23.4.0.8")])]});
            var Q75;
            Q75=makeQuery(id+"F1.opExtrude","SWEPT_FACE",FACE,{"disambiguationData":[OSD([sQuery(id+"F0.wireOp",EDGE,"E23.4.0.6")])]});
            var Q76;
            Q76=makeQuery(id+"F1.opExtrude","SWEPT_FACE",FACE,{"disambiguationData":[OSD([sQuery(id+"F0.wireOp",EDGE,"E23.3.0.9")])]});
            var Q77;
            Q77=makeQuery(id+"F1.opExtrude","SWEPT_FACE",FACE,{"disambiguationData":[OSD([sQuery(id+"F0.wireOp",EDGE,"E23.3.0.4")])]});
            var Q78;
            Q78=makeQuery(id+"F1.opExtrude","SWEPT_FACE",FACE,{"disambiguationData":[OSD([sQuery(id+"F0.wireOp",EDGE,"E23.3.0.5")])]});
            var Q79;
            Q79=makeQuery(id+"F1.opExtrude","SWEPT_FACE",FACE,{"disambiguationData":[OSD([sQuery(id+"F0.wireOp",EDGE,"E23.3.0.3")])]});
            var Q80;
            Q80=makeQuery(id+"F1.opExtrude","SWEPT_FACE",FACE,{"disambiguationData":[OSD([sQuery(id+"F0.wireOp",EDGE,"E23.4.0.5")])]});
            var Q81;
            Q81=makeQuery(id+"F1.opExtrude","SWEPT_FACE",FACE,{"disambiguationData":[OSD([sQuery(id+"F0.wireOp",EDGE,"E23.4.0.4")])]});
            var Q82;
            Q82=makeQuery(id+"F1.opExtrude","SWEPT_FACE",FACE,{"disambiguationData":[OSD([sQuery(id+"F0.wireOp",EDGE,"E23.4.0.9")])]});
            var Q83;
            Q83=makeQuery(id+"F1.opExtrude","SWEPT_FACE",FACE,{"disambiguationData":[OSD([sQuery(id+"F0.wireOp",EDGE,"E23.4.0.3")])]});
            var Q84;
            Q84=makeQuery(id+"F1.opExtrude","SWEPT_FACE",FACE,{"disambiguationData":[OSD([sQuery(id+"F0.wireOp",EDGE,"E23.5.0.8")])]});
            var Q85;
            Q85=makeQuery(id+"F1.opExtrude","SWEPT_FACE",FACE,{"disambiguationData":[OSD([sQuery(id+"F0.wireOp",EDGE,"E23.5.0.10")])]});
            var Q86;
            Q86=makeQuery(id+"F1.opExtrude","SWEPT_FACE",FACE,{"disambiguationData":[OSD([sQuery(id+"F0.wireOp",EDGE,"E23.5.0.7")])]});
            var Q87;
            Q87=makeQuery(id+"F1.opExtrude","SWEPT_FACE",FACE,{"disambiguationData":[OSD([sQuery(id+"F0.wireOp",EDGE,"E23.5.0.6")])]});
            var Q88;
            Q88=makeQuery(id+"F1.opExtrude","SWEPT_FACE",FACE,{"disambiguationData":[OSD([sQuery(id+"F0.wireOp",EDGE,"E23.5.0.3")])]});
            var Q89;
            Q89=makeQuery(id+"F1.opExtrude","SWEPT_FACE",FACE,{"disambiguationData":[OSD([sQuery(id+"F0.wireOp",EDGE,"E23.5.0.5")])]});
            var Q90;
            Q90=makeQuery(id+"F1.opExtrude","SWEPT_FACE",FACE,{"disambiguationData":[OSD([sQuery(id+"F0.wireOp",EDGE,"E23.5.0.4")])]});
            var Q91;
            Q91=makeQuery(id+"F1.opExtrude","SWEPT_FACE",FACE,{"disambiguationData":[OSD([sQuery(id+"F0.wireOp",EDGE,"E23.5.0.9")])]});
            chamfer(context, id + "F3", {"entities" : qUnion([Q0, Q1, Q2, Q3, Q4, Q5, Q6, Q7, Q8, Q9, Q10, Q11, Q12, Q13, Q14, Q15, Q16, Q17, Q18, Q19, Q20, Q21, Q22, Q23, Q24, Q25, Q26, Q27, Q28, Q29, Q30, Q31, Q32, Q33, Q34, Q35, Q36, Q37, Q38, Q39, Q40, Q41, Q42, Q43, Q44, Q45, Q46, Q47, Q48, Q49, Q50, Q51, Q52, Q53, Q54, Q55, Q56, Q57, Q58, Q59, Q60, Q61, Q62, Q63, Q64, Q65, Q66, Q67, Q68, Q69, Q70, Q71, Q72, Q73, Q74, Q75, Q76, Q77, Q78, Q79, Q80, Q81, Q82, Q83, Q84, Q85, Q86, Q87, Q88, Q89, Q90, Q91]), "width" : 0.5 * mm, "tangentPropagation" : true});
        }
        {
            var Q0;
            Q0=makeQuery(id+"F1.opExtrude","CAP_EDGE",EDGE,{"disambiguationData":[OSD([sQuery(id+"F0.wireOp",EDGE,"E51")])],"isStart":false});
            var Q1;
            Q1=makeQuery(id+"F1.opExtrude","CAP_EDGE",EDGE,{"disambiguationData":[OSD([sQuery(id+"F0.wireOp",EDGE,"E52")])],"isStart":false});
            var Q2;
            Q2=makeQuery(id+"F1.opExtrude","CAP_EDGE",EDGE,{"disambiguationData":[OSD([sQuery(id+"F0.wireOp",EDGE,"E54")])],"isStart":false});
            var Q3;
            Q3=makeQuery(id+"F1.opExtrude","CAP_EDGE",EDGE,{"disambiguationData":[OSD([sQuery(id+"F0.wireOp",EDGE,"E53.1.0.0")])],"isStart":false});
            var Q4;
            Q4=makeQuery(id+"F1.opExtrude","CAP_EDGE",EDGE,{"disambiguationData":[OSD([sQuery(id+"F0.wireOp",EDGE,"E53.1.0.1")])],"isStart":false});
            var Q5;
            Q5=makeQuery(id+"F1.opExtrude","CAP_EDGE",EDGE,{"disambiguationData":[OSD([sQuery(id+"F0.wireOp",EDGE,"E53.2.0.1")])],"isStart":false});
            var Q6;
            Q6=makeQuery(id+"F1.opExtrude","CAP_EDGE",EDGE,{"disambiguationData":[OSD([sQuery(id+"F0.wireOp",EDGE,"E53.2.0.0")])],"isStart":false});
            var Q7;
            Q7=makeQuery(id+"F1.opExtrude","CAP_EDGE",EDGE,{"disambiguationData":[OSD([sQuery(id+"F0.wireOp",EDGE,"E53.3.0.1")])],"isStart":false});
            var Q8;
            Q8=makeQuery(id+"F1.opExtrude","CAP_EDGE",EDGE,{"disambiguationData":[OSD([sQuery(id+"F0.wireOp",EDGE,"E53.3.0.0")])],"isStart":false});
            var Q9;
            Q9=makeQuery(id+"F1.opExtrude","CAP_EDGE",EDGE,{"disambiguationData":[OSD([sQuery(id+"F0.wireOp",EDGE,"E53.4.0.1")])],"isStart":false});
            var Q10;
            Q10=makeQuery(id+"F1.opExtrude","CAP_EDGE",EDGE,{"disambiguationData":[OSD([sQuery(id+"F0.wireOp",EDGE,"E53.4.0.0")])],"isStart":false});
            var Q11;
            Q11=makeQuery(id+"F1.opExtrude","CAP_EDGE",EDGE,{"disambiguationData":[OSD([sQuery(id+"F0.wireOp",EDGE,"E58")])],"isStart":false});
            var Q12;
            Q12=makeQuery(id+"F1.opExtrude","CAP_EDGE",EDGE,{"disambiguationData":[OSD([sQuery(id+"F0.wireOp",EDGE,"E53.5.0.0")])],"isStart":false});
            var Q13;
            Q13=makeQuery(id+"F1.opExtrude","CAP_EDGE",EDGE,{"disambiguationData":[OSD([sQuery(id+"F0.wireOp",EDGE,"E53.5.0.1")])],"isStart":false});
            var Q14;
            Q14=makeQuery(id+"F1.opExtrude","CAP_EDGE",EDGE,{"disambiguationData":[OSD([sQuery(id+"F0.wireOp",EDGE,"E53.6.0.0")])],"isStart":false});
            var Q15;
            Q15=makeQuery(id+"F1.opExtrude","CAP_EDGE",EDGE,{"disambiguationData":[OSD([sQuery(id+"F0.wireOp",EDGE,"E53.7.0.1")])],"isStart":false});
            var Q16;
            Q16=makeQuery(id+"F1.opExtrude","CAP_EDGE",EDGE,{"disambiguationData":[OSD([sQuery(id+"F0.wireOp",EDGE,"E53.6.0.1")])],"isStart":false});
            var Q17;
            Q17=makeQuery(id+"F1.opExtrude","CAP_EDGE",EDGE,{"disambiguationData":[OSD([sQuery(id+"F0.wireOp",EDGE,"E53.8.0.1")])],"isStart":false});
            var Q18;
            Q18=makeQuery(id+"F1.opExtrude","CAP_EDGE",EDGE,{"disambiguationData":[OSD([sQuery(id+"F0.wireOp",EDGE,"E53.8.0.0")])],"isStart":false});
            var Q19;
            Q19=makeQuery(id+"F1.opExtrude","CAP_EDGE",EDGE,{"disambiguationData":[OSD([sQuery(id+"F0.wireOp",EDGE,"E53.9.0.0")])],"isStart":false});
            var Q20;
            Q20=makeQuery(id+"F1.opExtrude","CAP_EDGE",EDGE,{"disambiguationData":[OSD([sQuery(id+"F0.wireOp",EDGE,"E53.9.0.1")])],"isStart":false});
            var Q21;
            Q21=makeQuery(id+"F1.opExtrude","CAP_EDGE",EDGE,{"disambiguationData":[OSD([sQuery(id+"F0.wireOp",EDGE,"E53.10.0.1")])],"isStart":false});
            var Q22;
            Q22=makeQuery(id+"F1.opExtrude","CAP_EDGE",EDGE,{"disambiguationData":[OSD([sQuery(id+"F0.wireOp",EDGE,"E57")])],"isStart":false});
            var Q23;
            Q23=makeQuery(id+"F1.opExtrude","CAP_EDGE",EDGE,{"disambiguationData":[OSD([sQuery(id+"F0.wireOp",EDGE,"E53.10.0.0")])],"isStart":false});
            var Q24;
            Q24=makeQuery(id+"F1.opExtrude","CAP_EDGE",EDGE,{"disambiguationData":[OSD([sQuery(id+"F0.wireOp",EDGE,"E53.11.0.1")])],"isStart":false});
            var Q25;
            Q25=makeQuery(id+"F1.opExtrude","CAP_EDGE",EDGE,{"disambiguationData":[OSD([sQuery(id+"F0.wireOp",EDGE,"E53.11.0.0")])],"isStart":false});
            var Q26;
            Q26=makeQuery(id+"F1.opExtrude","CAP_EDGE",EDGE,{"disambiguationData":[OSD([sQuery(id+"F0.wireOp",EDGE,"E53.12.0.0")])],"isStart":false});
            var Q27;
            Q27=makeQuery(id+"F1.opExtrude","CAP_EDGE",EDGE,{"disambiguationData":[OSD([sQuery(id+"F0.wireOp",EDGE,"E53.13.0.1")])],"isStart":false});
            var Q28;
            Q28=makeQuery(id+"F1.opExtrude","CAP_EDGE",EDGE,{"disambiguationData":[OSD([sQuery(id+"F0.wireOp",EDGE,"E53.13.0.0")])],"isStart":false});
            var Q29;
            Q29=makeQuery(id+"F1.opExtrude","CAP_EDGE",EDGE,{"disambiguationData":[OSD([sQuery(id+"F0.wireOp",EDGE,"E53.12.0.1")])],"isStart":false});
            var Q30;
            Q30=makeQuery(id+"F1.opExtrude","CAP_EDGE",EDGE,{"disambiguationData":[OSD([sQuery(id+"F0.wireOp",EDGE,"E53.14.0.1")])],"isStart":false});
            var Q31;
            Q31=makeQuery(id+"F1.opExtrude","CAP_EDGE",EDGE,{"disambiguationData":[OSD([sQuery(id+"F0.wireOp",EDGE,"E53.14.0.0")])],"isStart":false});
            var Q32;
            Q32=makeQuery(id+"F1.opExtrude","CAP_EDGE",EDGE,{"disambiguationData":[OSD([sQuery(id+"F0.wireOp",EDGE,"E56")])],"isStart":false});
            chamfer(context, id + "F4", {"entities" : qUnion([Q0, Q1, Q2, Q3, Q4, Q5, Q6, Q7, Q8, Q9, Q10, Q11, Q12, Q13, Q14, Q15, Q16, Q17, Q18, Q19, Q20, Q21, Q22, Q23, Q24, Q25, Q26, Q27, Q28, Q29, Q30, Q31, Q32]), "width" : 2.75 * mm, "tangentPropagation" : true});
        }
        {
            var Q0;
            Q0=makeQuery(id+"F1.opExtrude","CAP_EDGE",EDGE,{"disambiguationData":[OSD([sQuery(id+"F0.wireOp",EDGE,"E52")])],"isStart":true});
            var Q1;
            Q1=makeQuery(id+"F1.opExtrude","CAP_EDGE",EDGE,{"disambiguationData":[OSD([sQuery(id+"F0.wireOp",EDGE,"E54")])],"isStart":true});
            var Q2;
            Q2=makeQuery(id+"F1.opExtrude","CAP_EDGE",EDGE,{"disambiguationData":[OSD([sQuery(id+"F0.wireOp",EDGE,"E53.1.0.0")])],"isStart":true});
            var Q3;
            Q3=makeQuery(id+"F1.opExtrude","CAP_EDGE",EDGE,{"disambiguationData":[OSD([sQuery(id+"F0.wireOp",EDGE,"E51")])],"isStart":true});
            var Q4;
            Q4=makeQuery(id+"F1.opExtrude","CAP_EDGE",EDGE,{"disambiguationData":[OSD([sQuery(id+"F0.wireOp",EDGE,"E53.2.0.1")])],"isStart":true});
            var Q5;
            Q5=makeQuery(id+"F1.opExtrude","CAP_EDGE",EDGE,{"disambiguationData":[OSD([sQuery(id+"F0.wireOp",EDGE,"E53.3.0.1")])],"isStart":true});
            var Q6;
            Q6=makeQuery(id+"F1.opExtrude","CAP_EDGE",EDGE,{"disambiguationData":[OSD([sQuery(id+"F0.wireOp",EDGE,"E53.3.0.0")])],"isStart":true});
            var Q7;
            Q7=makeQuery(id+"F1.opExtrude","CAP_EDGE",EDGE,{"disambiguationData":[OSD([sQuery(id+"F0.wireOp",EDGE,"E53.2.0.0")])],"isStart":true});
            var Q8;
            Q8=makeQuery(id+"F1.opExtrude","CAP_EDGE",EDGE,{"disambiguationData":[OSD([sQuery(id+"F0.wireOp",EDGE,"E53.1.0.1")])],"isStart":true});
            var Q9;
            Q9=makeQuery(id+"F1.opExtrude","CAP_EDGE",EDGE,{"disambiguationData":[OSD([sQuery(id+"F0.wireOp",EDGE,"E53.4.0.1")])],"isStart":true});
            var Q10;
            Q10=makeQuery(id+"F1.opExtrude","CAP_EDGE",EDGE,{"disambiguationData":[OSD([sQuery(id+"F0.wireOp",EDGE,"E53.5.0.1")])],"isStart":true});
            var Q11;
            Q11=makeQuery(id+"F1.opExtrude","CAP_EDGE",EDGE,{"disambiguationData":[OSD([sQuery(id+"F0.wireOp",EDGE,"E53.6.0.1")])],"isStart":true});
            var Q12;
            Q12=makeQuery(id+"F1.opExtrude","CAP_EDGE",EDGE,{"disambiguationData":[OSD([sQuery(id+"F0.wireOp",EDGE,"E53.7.0.1")])],"isStart":true});
            var Q13;
            Q13=makeQuery(id+"F1.opExtrude","CAP_EDGE",EDGE,{"disambiguationData":[OSD([sQuery(id+"F0.wireOp",EDGE,"E53.8.0.1")])],"isStart":true});
            var Q14;
            Q14=makeQuery(id+"F1.opExtrude","CAP_EDGE",EDGE,{"disambiguationData":[OSD([sQuery(id+"F0.wireOp",EDGE,"E53.7.0.0")])],"isStart":true});
            var Q15;
            Q15=makeQuery(id+"F1.opExtrude","CAP_EDGE",EDGE,{"disambiguationData":[OSD([sQuery(id+"F0.wireOp",EDGE,"E53.6.0.0")])],"isStart":true});
            var Q16;
            Q16=makeQuery(id+"F1.opExtrude","CAP_EDGE",EDGE,{"disambiguationData":[OSD([sQuery(id+"F0.wireOp",EDGE,"E53.5.0.0")])],"isStart":true});
            var Q17;
            Q17=makeQuery(id+"F1.opExtrude","CAP_EDGE",EDGE,{"disambiguationData":[OSD([sQuery(id+"F0.wireOp",EDGE,"E53.4.0.0")])],"isStart":true});
            var Q18;
            Q18=makeQuery(id+"F1.opExtrude","CAP_EDGE",EDGE,{"disambiguationData":[OSD([sQuery(id+"F0.wireOp",EDGE,"E55")])],"isStart":true});
            var Q19;
            Q19=makeQuery(id+"F1.opExtrude","CAP_EDGE",EDGE,{"disambiguationData":[OSD([sQuery(id+"F0.wireOp",EDGE,"E53.9.0.1")])],"isStart":true});
            var Q20;
            Q20=makeQuery(id+"F1.opExtrude","CAP_EDGE",EDGE,{"disambiguationData":[OSD([sQuery(id+"F0.wireOp",EDGE,"E53.8.0.0")])],"isStart":true});
            var Q21;
            Q21=makeQuery(id+"F1.opExtrude","CAP_EDGE",EDGE,{"disambiguationData":[OSD([sQuery(id+"F0.wireOp",EDGE,"E53.9.0.0")])],"isStart":true});
            var Q22;
            Q22=makeQuery(id+"F1.opExtrude","CAP_EDGE",EDGE,{"disambiguationData":[OSD([sQuery(id+"F0.wireOp",EDGE,"E53.10.0.1")])],"isStart":true});
            var Q23;
            Q23=makeQuery(id+"F1.opExtrude","CAP_EDGE",EDGE,{"disambiguationData":[OSD([sQuery(id+"F0.wireOp",EDGE,"E53.10.0.0")])],"isStart":true});
            var Q24;
            Q24=makeQuery(id+"F1.opExtrude","CAP_EDGE",EDGE,{"disambiguationData":[OSD([sQuery(id+"F0.wireOp",EDGE,"E53.11.0.1")])],"isStart":true});
            var Q25;
            Q25=makeQuery(id+"F1.opExtrude","CAP_EDGE",EDGE,{"disambiguationData":[OSD([sQuery(id+"F0.wireOp",EDGE,"E53.11.0.0")])],"isStart":true});
            var Q26;
            Q26=makeQuery(id+"F1.opExtrude","CAP_EDGE",EDGE,{"disambiguationData":[OSD([sQuery(id+"F0.wireOp",EDGE,"E57")])],"isStart":true});
            var Q27;
            Q27=makeQuery(id+"F1.opExtrude","CAP_EDGE",EDGE,{"disambiguationData":[OSD([sQuery(id+"F0.wireOp",EDGE,"E53.12.0.1")])],"isStart":true});
            var Q28;
            Q28=makeQuery(id+"F1.opExtrude","CAP_EDGE",EDGE,{"disambiguationData":[OSD([sQuery(id+"F0.wireOp",EDGE,"E53.13.0.1")])],"isStart":true});
            var Q29;
            Q29=makeQuery(id+"F1.opExtrude","CAP_EDGE",EDGE,{"disambiguationData":[OSD([sQuery(id+"F0.wireOp",EDGE,"E53.14.0.1")])],"isStart":true});
            var Q30;
            Q30=makeQuery(id+"F1.opExtrude","CAP_EDGE",EDGE,{"disambiguationData":[OSD([sQuery(id+"F0.wireOp",EDGE,"E56")])],"isStart":true});
            var Q31;
            Q31=makeQuery(id+"F1.opExtrude","CAP_EDGE",EDGE,{"disambiguationData":[OSD([sQuery(id+"F0.wireOp",EDGE,"E53.12.0.0")])],"isStart":true});
            var Q32;
            Q32=makeQuery(id+"F1.opExtrude","CAP_EDGE",EDGE,{"disambiguationData":[OSD([sQuery(id+"F0.wireOp",EDGE,"E53.13.0.0")])],"isStart":true});
            var Q33;
            Q33=makeQuery(id+"F1.opExtrude","CAP_EDGE",EDGE,{"disambiguationData":[OSD([sQuery(id+"F0.wireOp",EDGE,"E53.14.0.0")])],"isStart":true});
            var Q34;
            Q34=makeQuery(id+"F1.opExtrude","CAP_EDGE",EDGE,{"disambiguationData":[OSD([sQuery(id+"F0.wireOp",EDGE,"E58")])],"isStart":true});
            var Q35;
            Q35=makeQuery(id+"F1.opExtrude","CAP_EDGE",EDGE,{"disambiguationData":[OSD([sQuery(id+"F0.wireOp",EDGE,"E60")])],"isStart":true});
            var Q36;
            Q36=makeQuery(id+"F1.opExtrude","CAP_EDGE",EDGE,{"disambiguationData":[OSD([sQuery(id+"F0.wireOp",EDGE,"E59")])],"isStart":true});
            var Q37;
            Q37=makeQuery(id+"F1.opExtrude","CAP_EDGE",EDGE,{"disambiguationData":[OSD([sQuery(id+"F0.wireOp",EDGE,"E59")])],"isStart":false});
            var Q38;
            Q38=makeQuery(id+"F1.opExtrude","CAP_EDGE",EDGE,{"disambiguationData":[OSD([sQuery(id+"F0.wireOp",EDGE,"E55")])],"isStart":false});
            var Q39;
            Q39=makeQuery(id+"F1.opExtrude","CAP_EDGE",EDGE,{"disambiguationData":[OSD([sQuery(id+"F0.wireOp",EDGE,"E60")])],"isStart":false});
            var Q40;
            Q40=makeQuery(id+"F1.opExtrude","CAP_EDGE",EDGE,{"disambiguationData":[OSD([sQuery(id+"F0.wireOp",EDGE,"E53.7.0.0")])],"isStart":false});
            chamfer(context, id + "F5", {"entities" : qUnion([Q0, Q1, Q2, Q3, Q4, Q5, Q6, Q7, Q8, Q9, Q10, Q11, Q12, Q13, Q14, Q15, Q16, Q17, Q18, Q19, Q20, Q21, Q22, Q23, Q24, Q25, Q26, Q27, Q28, Q29, Q30, Q31, Q32, Q33, Q34, Q35, Q36, Q37, Q38, Q39, Q40]), "width" : 0.5 * mm, "tangentPropagation" : true});
        }
    });
